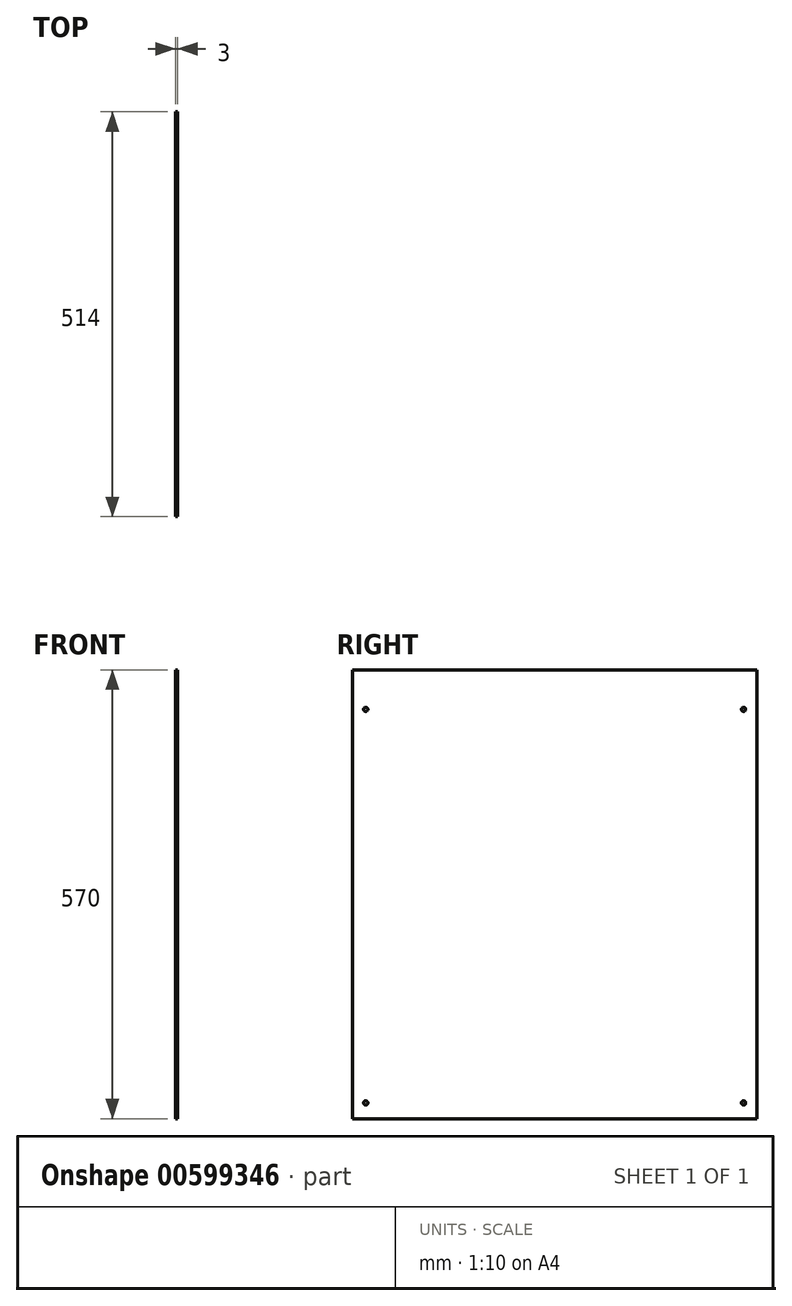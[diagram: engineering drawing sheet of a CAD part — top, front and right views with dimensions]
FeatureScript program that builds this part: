
annotation { "Feature Type Name" : "Feature", "Feature Type Description" : "" }
export const myFeature = defineFeature(function(context is Context, id is Id, definition is map)
    precondition{}
    {
        {
            var Q0;
            Q0=qCreatedBy(makeId("Right.planeOp"),FACE);
            var sketch = newSketch(context, id + "F0", { "sketchPlane" : qUnion([Q0])});
            skLineSegment(sketch, "E0.bottom", {"start": v(-250, 260) * mm, "end": v(250, 260) * mm});
            skLineSegment(sketch, "E0.top", {"start": v(-250, -260) * mm, "end": v(250, -260) * mm, "construction": true});
            skLineSegment(sketch, "E0.left", {"start": v(-250, 260) * mm, "end": v(-250, -260) * mm});
            skLineSegment(sketch, "E0.right", {"start": v(250, 260) * mm, "end": v(250, -260) * mm});
            skCircle(sketch, "E1", {"center": v(-240, 250) * mm, "radius": 2.65 * mm});
            skCircle(sketch, "E2", {"center": v(-240, -250) * mm, "radius": 2.65 * mm});
            skCircle(sketch, "E3", {"center": v(240, -250) * mm, "radius": 2.65 * mm});
            skCircle(sketch, "E4", {"center": v(240, 250) * mm, "radius": 2.65 * mm});
            skLineSegment(sketch, "E5.top", {"start": v(-250, 300) * mm, "end": v(250, 300) * mm});
            skLineSegment(sketch, "E5.left", {"start": v(-250, 260) * mm, "end": v(-250, 300) * mm});
            skLineSegment(sketch, "E5.right", {"start": v(250, 260) * mm, "end": v(250, 300) * mm});
            skLineSegment(sketch, "E6.bottom", {"start": v(250, 300) * mm, "end": v(257, 300) * mm});
            skLineSegment(sketch, "E6.top", {"start": v(250, -260) * mm, "end": v(257, -260) * mm, "construction": true});
            skLineSegment(sketch, "E6.left", {"start": v(250, 300) * mm, "end": v(250, -260) * mm});
            skLineSegment(sketch, "E6.right", {"start": v(257, 300) * mm, "end": v(257, -260) * mm});
            skLineSegment(sketch, "E7.bottom", {"start": v(-250, 300) * mm, "end": v(-257, 300) * mm});
            skLineSegment(sketch, "E7.top", {"start": v(-250, -260) * mm, "end": v(-257, -260) * mm, "construction": true});
            skLineSegment(sketch, "E7.left", {"start": v(-250, 300) * mm, "end": v(-250, -260) * mm});
            skLineSegment(sketch, "E7.right", {"start": v(-257, 300) * mm, "end": v(-257, -260) * mm});
            skLineSegment(sketch, "E8", {"start": v(-257, -260) * mm, "end": v(-257, -270) * mm});
            skLineSegment(sketch, "E9", {"start": v(-257, -270) * mm, "end": v(257, -270) * mm});
            skLineSegment(sketch, "E10", {"start": v(257, -270) * mm, "end": v(257, -260) * mm});
            skSolve(sketch);
        }
        {
            var Q0;
            Q0=qSketchRegion(id+"F0",true);
            extrude(context, id + "F1", {"entities" : qUnion([Q0]), "depth" : 3 * mm});
        }
    });
